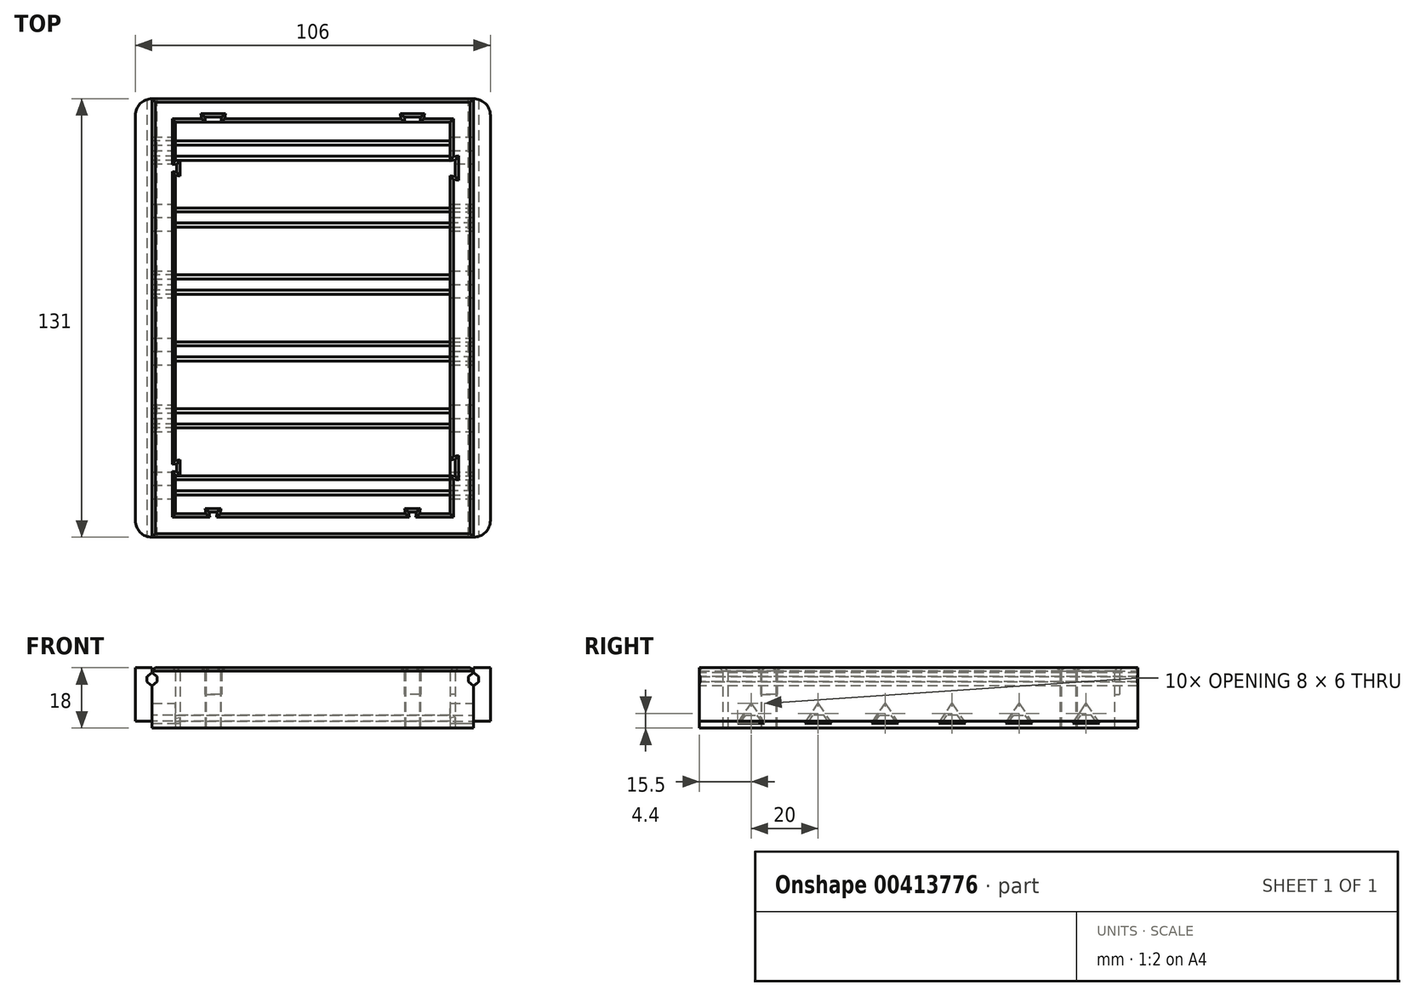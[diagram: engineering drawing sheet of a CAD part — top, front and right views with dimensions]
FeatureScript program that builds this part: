
annotation { "Feature Type Name" : "Feature", "Feature Type Description" : "" }
export const myFeature = defineFeature(function(context is Context, id is Id, definition is map)
    precondition{}
    {
        {
            var Q0;
            Q0=qCreatedBy(makeId("Top.planeOp"),FACE);
            var sketch = newSketch(context, id + "F0", { "sketchPlane" : qUnion([Q0])});
            skLineSegment(sketch, "E0.bottom", {"start": v(41, 58.5) * mm, "end": v(-41, 58.5) * mm});
            skLineSegment(sketch, "E0.top", {"start": v(41, -58.5) * mm, "end": v(-41, -58.5) * mm});
            skLineSegment(sketch, "E0.left", {"start": v(41, 58.5) * mm, "end": v(41, -58.5) * mm});
            skLineSegment(sketch, "E0.right", {"start": v(-41, 58.5) * mm, "end": v(-41, -58.5) * mm});
            skPoint(sketch, "E0.middle", {"position": v(0, 0) * mm});
            skPoint(sketch, "E1", {"position": v(41, 47) * mm});
            skPoint(sketch, "E2", {"position": v(41, 42.5) * mm});
            skLineSegment(sketch, "E3", {"start": v(41, 47) * mm, "end": v(41, 42.5) * mm});
            skLineSegment(sketch, "E4", {"start": v(42.5, 47.25) * mm, "end": v(42.5, 42.25) * mm});
            skPoint(sketch, "E5", {"position": v(41, 44.75) * mm});
            skPoint(sketch, "E6", {"position": v(42.5, 44.75) * mm});
            skLineSegment(sketch, "E7", {"start": v(42.5, 42.25) * mm, "end": v(41, 42.5) * mm});
            skLineSegment(sketch, "E8", {"start": v(41, 47) * mm, "end": v(42.5, 47.25) * mm});
            skLineSegment(sketch, "E9.MirrorCS", {"start": v(42.5, -42.25) * mm, "end": v(41, -42.5) * mm});
            skLineSegment(sketch, "E10.MirrorCS", {"start": v(42.5, -47.25) * mm, "end": v(42.5, -42.25) * mm});
            skLineSegment(sketch, "E11.MirrorCS", {"start": v(41, -47) * mm, "end": v(42.5, -47.25) * mm});
            skLineSegment(sketch, "E12.MirrorCS", {"start": v(41, -47) * mm, "end": v(41, -42.5) * mm});
            skLineSegment(sketch, "E13", {"start": v(-32, 58.5) * mm, "end": v(-32.25, 60) * mm});
            skLineSegment(sketch, "E14", {"start": v(-32.25, 60) * mm, "end": v(-27.25, 60) * mm});
            skLineSegment(sketch, "E15", {"start": v(-27.25, 60) * mm, "end": v(-27.5, 58.5) * mm});
            skPoint(sketch, "E16", {"position": v(-29.75, 60) * mm});
            skLineSegment(sketch, "E17", {"start": v(-32, 58.5) * mm, "end": v(-27.5, 58.5) * mm, "construction": true});
            skPoint(sketch, "E18", {"position": v(-29.75, 58.5) * mm});
            skLineSegment(sketch, "E19.MirrorCS", {"start": v(27.25, 60) * mm, "end": v(27.5, 58.5) * mm});
            skLineSegment(sketch, "E20.MirrorCS", {"start": v(32.25, 60) * mm, "end": v(27.25, 60) * mm});
            skLineSegment(sketch, "E21.MirrorCS", {"start": v(32, 58.5) * mm, "end": v(32.25, 60) * mm});
            skLineSegment(sketch, "E22.MirrorCS", {"start": v(32, 58.5) * mm, "end": v(27.5, 58.5) * mm, "construction": true});
            skLineSegment(sketch, "E23", {"start": v(-41, 46.9) * mm, "end": v(-39.7, 47.1) * mm});
            skLineSegment(sketch, "E24", {"start": v(-39.7, 47.1) * mm, "end": v(-39.7, 42.4) * mm});
            skLineSegment(sketch, "E25", {"start": v(-39.7, 42.4) * mm, "end": v(-41, 42.6) * mm});
            skPoint(sketch, "E26", {"position": v(-39.7, 44.75) * mm});
            skLineSegment(sketch, "E27", {"start": v(-41, 42.6) * mm, "end": v(-41, 46.9) * mm, "construction": true});
            skPoint(sketch, "E28", {"position": v(-41, 44.75) * mm});
            skLineSegment(sketch, "E29.MirrorCS", {"start": v(-39.7, -42.4) * mm, "end": v(-41, -42.6) * mm});
            skLineSegment(sketch, "E30.MirrorCS", {"start": v(-39.7, -47.1) * mm, "end": v(-39.7, -42.4) * mm});
            skLineSegment(sketch, "E31.MirrorCS", {"start": v(-41, -46.9) * mm, "end": v(-39.7, -47.1) * mm});
            skPoint(sketch, "E32", {"position": v(-29.75, -58.5) * mm});
            skLineSegment(sketch, "E33", {"start": v(-31.9, -58.5) * mm, "end": v(-27.6, -58.5) * mm, "construction": true});
            skLineSegment(sketch, "E34", {"start": v(-32.1, -57) * mm, "end": v(-27.4, -57) * mm});
            skPoint(sketch, "E35", {"position": v(-29.75, -57) * mm});
            skLineSegment(sketch, "E36", {"start": v(-32.1, -57) * mm, "end": v(-31.9, -58.5) * mm});
            skLineSegment(sketch, "E37", {"start": v(-27.6, -58.5) * mm, "end": v(-27.4, -57) * mm});
            skLineSegment(sketch, "E38.MirrorCS", {"start": v(27.6, -58.5) * mm, "end": v(27.4, -57) * mm});
            skLineSegment(sketch, "E39.MirrorCS", {"start": v(32.1, -57) * mm, "end": v(27.4, -57) * mm});
            skLineSegment(sketch, "E40.0", {"start": v(-48, 65.5) * mm, "end": v(-48, -65.5) * mm});
            skLineSegment(sketch, "E40.1", {"start": v(48, 65.5) * mm, "end": v(-48, 65.5) * mm});
            skLineSegment(sketch, "E40.2", {"start": v(48, 65.5) * mm, "end": v(48, -65.5) * mm});
            skLineSegment(sketch, "E40.3", {"start": v(48, -65.5) * mm, "end": v(-48, -65.5) * mm});
            skLineSegment(sketch, "E41.MirrorCS", {"start": v(31.9, -58.5) * mm, "end": v(27.6, -58.5) * mm, "construction": true});
            skLineSegment(sketch, "E42", {"start": v(32.1, -57) * mm, "end": v(31.9, -58.5) * mm});
            skSolve(sketch);
        }
        {
            var Q0;
            Q0 = qSketchRegion(id + "F0", true);
            var Q1;
            {var subQ0=sQuery(id+"F0.wireOp",EDGE,"E29.MirrorCS");Q1=makeQuery(id+"F0.imprint","IMPRINT",FACE,{"disambiguationData":[TD([[makeQuery(id+"F0.imprint","IMPRINT",EDGE,{"derivedFrom":subQ0}),1.0]])]});}
            var Q2;
            Q2=makeQuery(id+"F0.imprint","IMPRINT",FACE,{"disambiguationData":[TD([[makeQuery(id+"F0.imprint","IMPRINT",EDGE,{"derivedFrom":sQuery(id+"F0.wireOp",EDGE,"E34")}),-1.0]])]});
            var Q3;
            Q3=makeQuery(id+"F0.imprint","IMPRINT",FACE,{"disambiguationData":[TD([[makeQuery(id+"F0.imprint","IMPRINT",EDGE,{"derivedFrom":sQuery(id+"F0.wireOp",EDGE,"E39.MirrorCS")}),1.0]])]});
            var Q4;
            {var subQ0=sQuery(id+"F0.wireOp",EDGE,"E23");Q4=makeQuery(id+"F0.imprint","IMPRINT",FACE,{"disambiguationData":[TD([[makeQuery(id+"F0.imprint","IMPRINT",EDGE,{"derivedFrom":subQ0}),-1.0]])]});}
            extrude(context, id + "F1", {"entities" : qUnion([Q0, Q1, Q2, Q3, Q4]), "depth" : 8 * mm});
        }
        {
            var Q0;
            Q0=makeQuery(id+"F0.imprint","IMPRINT",FACE,{"disambiguationData":[TD([[makeQuery(id+"F0.imprint","IMPRINT",EDGE,{"derivedFrom":sQuery(id+"F0.wireOp",EDGE,"E4")}),1.0]])]});
            var Q1;
            Q1=makeQuery(id+"F0.imprint","IMPRINT",FACE,{"disambiguationData":[TD([[makeQuery(id+"F0.imprint","IMPRINT",EDGE,{"derivedFrom":sQuery(id+"F0.wireOp",EDGE,"E9.MirrorCS")}),1.0]])]});
            var Q2;
            {var subQ0=sQuery(id+"F0.wireOp",EDGE,"E19.MirrorCS");Q2=makeQuery(id+"F0.imprint","IMPRINT",FACE,{"disambiguationData":[TD([[makeQuery(id+"F0.imprint","IMPRINT",EDGE,{"derivedFrom":subQ0}),1.0]])]});}
            var Q3;
            {var subQ0=sQuery(id+"F0.wireOp",EDGE,"E13");Q3=makeQuery(id+"F0.imprint","IMPRINT",FACE,{"disambiguationData":[TD([[makeQuery(id+"F0.imprint","IMPRINT",EDGE,{"derivedFrom":subQ0}),-1.0]])]});}
            var Q4;
            Q4=makeQuery(id+"F0.imprint","IMPRINT",FACE,{"disambiguationData":[TD([[makeQuery(id+"F0.imprint","IMPRINT",EDGE,{"derivedFrom":sQuery(id+"F0.wireOp",EDGE,"E34")}),-1.0]])]});
            var Q5;
            {var subQ0=sQuery(id+"F0.wireOp",EDGE,"E29.MirrorCS");Q5=makeQuery(id+"F0.imprint","IMPRINT",FACE,{"disambiguationData":[TD([[makeQuery(id+"F0.imprint","IMPRINT",EDGE,{"derivedFrom":subQ0}),1.0]])]});}
            var Q6;
            Q6=makeQuery(id+"F0.imprint","IMPRINT",FACE,{"disambiguationData":[TD([[makeQuery(id+"F0.imprint","IMPRINT",EDGE,{"derivedFrom":sQuery(id+"F0.wireOp",EDGE,"E39.MirrorCS")}),1.0]])]});
            var Q7;
            Q7=makeQuery(id+"F0.imprint","IMPRINT",FACE,{"disambiguationData":[TD([[makeQuery(id+"F0.imprint","IMPRINT",EDGE,{"derivedFrom":sQuery(id+"F0.wireOp",EDGE,"E3")}),1.0]])]});
            var Q8;
            {var subQ1=sQuery(id+"F0.wireOp",EDGE,"E3");Q8=makeQuery(id+"F0.imprint","IMPRINT",FACE,{"disambiguationData":[TD([[makeQuery(id+"F0.imprint","IMPRINT",EDGE,{"derivedFrom":subQ1}),-1.0]])]});}
            var Q9;
            {var subQ0=sQuery(id+"F0.wireOp",EDGE,"E23");Q9=makeQuery(id+"F0.imprint","IMPRINT",FACE,{"disambiguationData":[TD([[makeQuery(id+"F0.imprint","IMPRINT",EDGE,{"derivedFrom":subQ0}),-1.0]])]});}
            extrude(context, id + "F2", {"entities" : qUnion([Q0, Q1, Q2, Q3, Q4, Q5, Q6, Q7, Q8, Q9]), "operationType" : NewBodyOperationType.ADD, "oppositeDirection" : true, "depth" : 8 * mm});
        }
        {
            var Q0;
            Q0=makeQuery(id+"F2.opExtrude","CAP_FACE",FACE,{"disambiguationData":[OSD([sQuery(id+"F0.wireOp",EDGE,"E40.0"),sQuery(id+"F0.wireOp",EDGE,"E40.1"),sQuery(id+"F0.wireOp",EDGE,"E40.2"),sQuery(id+"F0.wireOp",EDGE,"E40.3")])],"isStart":false});
            extrude(context, id + "F3", {"entities" : qUnion([Q0]), "operationType" : NewBodyOperationType.ADD, "depth" : 2 * mm});
        }
        {
            var Q0;
            {var subQ0=sQuery(id+"F0.wireOp",EDGE,"E40.2");Q0=makeQuery(id+"F2.boolean.opBoolean","MERGE",FACE,{"derivedFrom":[makeQuery(id+"F1.opExtrude","SWEPT_FACE",FACE,{"disambiguationData":[OSD([subQ0])]}),makeQuery(id+"F2.opExtrude","SWEPT_FACE",FACE,{"disambiguationData":[OSD([subQ0])]})]});}
            var sketch = newSketch(context, id + "F4", { "sketchPlane" : qUnion([Q0])});
            skLineSegment(sketch, "E43", {"start": v(-54, -8.6) * mm, "end": v(-50, -2.6) * mm});
            skLineSegment(sketch, "E44", {"start": v(-50, -2.6) * mm, "end": v(-46, -8.6) * mm});
            skLineSegment(sketch, "E45", {"start": v(-46, -8.6) * mm, "end": v(-54, -8.6) * mm});
            skPoint(sketch, "E46", {"position": v(-50, -8.6) * mm});
            skLineSegment(sketch, "E47.0", {"start": v(-52.88, -8) * mm, "end": v(-50, -3.68) * mm});
            skLineSegment(sketch, "E47.1", {"start": v(-47.12, -8) * mm, "end": v(-52.88, -8) * mm});
            skLineSegment(sketch, "E47.2", {"start": v(-50, -3.68) * mm, "end": v(-47.12, -8) * mm});
            skLineSegment(sketch, "E48.1.0.0", {"start": v(-30, -2.6) * mm, "end": v(-26, -8.6) * mm});
            skLineSegment(sketch, "E48.1.0.1", {"start": v(-30, -3.68) * mm, "end": v(-27.12, -8) * mm});
            skLineSegment(sketch, "E48.1.0.2", {"start": v(-34, -8.6) * mm, "end": v(-30, -2.6) * mm});
            skLineSegment(sketch, "E48.1.0.3", {"start": v(-32.88, -8) * mm, "end": v(-30, -3.68) * mm});
            skLineSegment(sketch, "E48.1.0.4", {"start": v(-27.12, -8) * mm, "end": v(-32.88, -8) * mm});
            skLineSegment(sketch, "E48.1.0.5", {"start": v(-26, -8.6) * mm, "end": v(-34, -8.6) * mm});
            skLineSegment(sketch, "E48.2.0.0", {"start": v(-10, -2.6) * mm, "end": v(-6, -8.6) * mm});
            skLineSegment(sketch, "E48.2.0.1", {"start": v(-10, -3.68) * mm, "end": v(-7.12, -8) * mm});
            skLineSegment(sketch, "E48.2.0.2", {"start": v(-14, -8.6) * mm, "end": v(-10, -2.6) * mm});
            skLineSegment(sketch, "E48.2.0.3", {"start": v(-12.88, -8) * mm, "end": v(-10, -3.68) * mm});
            skLineSegment(sketch, "E48.2.0.4", {"start": v(-7.12, -8) * mm, "end": v(-12.88, -8) * mm});
            skLineSegment(sketch, "E48.2.0.5", {"start": v(-6, -8.6) * mm, "end": v(-14, -8.6) * mm});
            skLineSegment(sketch, "E48.3.0.0", {"start": v(10, -2.6) * mm, "end": v(14, -8.6) * mm});
            skLineSegment(sketch, "E48.3.0.1", {"start": v(10, -3.68) * mm, "end": v(12.88, -8) * mm});
            skLineSegment(sketch, "E48.3.0.2", {"start": v(6, -8.6) * mm, "end": v(10, -2.6) * mm});
            skLineSegment(sketch, "E48.3.0.3", {"start": v(7.12, -8) * mm, "end": v(10, -3.68) * mm});
            skLineSegment(sketch, "E48.3.0.4", {"start": v(12.88, -8) * mm, "end": v(7.12, -8) * mm});
            skLineSegment(sketch, "E48.3.0.5", {"start": v(14, -8.6) * mm, "end": v(6, -8.6) * mm});
            skLineSegment(sketch, "E48.4.0.0", {"start": v(30, -2.6) * mm, "end": v(34, -8.6) * mm});
            skLineSegment(sketch, "E48.4.0.1", {"start": v(30, -3.68) * mm, "end": v(32.88, -8) * mm});
            skLineSegment(sketch, "E48.4.0.2", {"start": v(26, -8.6) * mm, "end": v(30, -2.6) * mm});
            skLineSegment(sketch, "E48.4.0.3", {"start": v(27.12, -8) * mm, "end": v(30, -3.68) * mm});
            skLineSegment(sketch, "E48.4.0.4", {"start": v(32.88, -8) * mm, "end": v(27.12, -8) * mm});
            skLineSegment(sketch, "E48.4.0.5", {"start": v(34, -8.6) * mm, "end": v(26, -8.6) * mm});
            skLineSegment(sketch, "E48.5.0.0", {"start": v(50, -2.6) * mm, "end": v(54, -8.6) * mm});
            skLineSegment(sketch, "E48.5.0.1", {"start": v(50, -3.68) * mm, "end": v(52.88, -8) * mm});
            skLineSegment(sketch, "E48.5.0.2", {"start": v(46, -8.6) * mm, "end": v(50, -2.6) * mm});
            skLineSegment(sketch, "E48.5.0.3", {"start": v(47.12, -8) * mm, "end": v(50, -3.68) * mm});
            skLineSegment(sketch, "E48.5.0.4", {"start": v(52.88, -8) * mm, "end": v(47.12, -8) * mm});
            skLineSegment(sketch, "E48.5.0.5", {"start": v(54, -8.6) * mm, "end": v(46, -8.6) * mm});
            skLineSegment(sketch, "E48.direction1", {"start": v(-46, -8.6) * mm, "end": v(-26, -8.6) * mm, "construction": true});
            skCircle(sketch, "E49", {"center": v(0, -4) * mm, "radius": 2.5 * mm});
            skPoint(sketch, "E49.centerSnap0", {"position": v(0, -10) * mm});
            skLineSegment(sketch, "E50", {"start": v(0.75, -1.62) * mm, "end": v(0.75, -6.38) * mm});
            skLineSegment(sketch, "E51", {"start": v(-0.75, -1.62) * mm, "end": v(-0.75, -6.38) * mm});
            skLineSegment(sketch, "E52", {"start": v(-65.5, -8) * mm, "end": v(65.5, -8) * mm});
            skLineSegment(sketch, "E53", {"start": v(-54, -8.6) * mm, "end": v(-65.5, -8.6) * mm, "construction": true});
            skLineSegment(sketch, "E54", {"start": v(54, -8.6) * mm, "end": v(65.5, -8.6) * mm, "construction": true});
            skSolve(sketch);
        }
        {
            var Q0;
            Q0=makeQuery(id+"F4.imprint","IMPRINT",FACE,{"disambiguationData":[TD([[makeQuery(id+"F4.imprint","IMPRINT",EDGE,{"derivedFrom":sQuery(id+"F4.wireOp",EDGE,"E43")}),-1.0]])]});
            var Q1;
            Q1=makeQuery(id+"F4.imprint","IMPRINT",FACE,{"disambiguationData":[TD([[makeQuery(id+"F4.imprint","IMPRINT",EDGE,{"derivedFrom":sQuery(id+"F4.wireOp",EDGE,"E47.0")}),-1.0]])]});
            var Q2;
            Q2=makeQuery(id+"F4.imprint","IMPRINT",FACE,{"disambiguationData":[TD([[makeQuery(id+"F4.imprint","IMPRINT",EDGE,{"derivedFrom":sQuery(id+"F4.wireOp",EDGE,"E48.1.0.0")}),-1.0]])]});
            var Q3;
            Q3=makeQuery(id+"F4.imprint","IMPRINT",FACE,{"disambiguationData":[TD([[makeQuery(id+"F4.imprint","IMPRINT",EDGE,{"derivedFrom":sQuery(id+"F4.wireOp",EDGE,"E48.1.0.1")}),-1.0]])]});
            var Q4;
            Q4=makeQuery(id+"F4.imprint","IMPRINT",FACE,{"disambiguationData":[TD([[makeQuery(id+"F4.imprint","IMPRINT",EDGE,{"derivedFrom":sQuery(id+"F4.wireOp",EDGE,"E48.2.0.0")}),-1.0]])]});
            var Q5;
            Q5=makeQuery(id+"F4.imprint","IMPRINT",FACE,{"disambiguationData":[TD([[makeQuery(id+"F4.imprint","IMPRINT",EDGE,{"derivedFrom":sQuery(id+"F4.wireOp",EDGE,"E48.2.0.1")}),-1.0]])]});
            var Q6;
            Q6=makeQuery(id+"F4.imprint","IMPRINT",FACE,{"disambiguationData":[TD([[makeQuery(id+"F4.imprint","IMPRINT",EDGE,{"derivedFrom":sQuery(id+"F4.wireOp",EDGE,"E48.3.0.1")}),-1.0]])]});
            var Q7;
            Q7=makeQuery(id+"F4.imprint","IMPRINT",FACE,{"disambiguationData":[TD([[makeQuery(id+"F4.imprint","IMPRINT",EDGE,{"derivedFrom":sQuery(id+"F4.wireOp",EDGE,"E48.3.0.0")}),-1.0]])]});
            var Q8;
            Q8=makeQuery(id+"F4.imprint","IMPRINT",FACE,{"disambiguationData":[TD([[makeQuery(id+"F4.imprint","IMPRINT",EDGE,{"derivedFrom":sQuery(id+"F4.wireOp",EDGE,"E48.5.0.1")}),-1.0]])]});
            var Q9;
            Q9=makeQuery(id+"F4.imprint","IMPRINT",FACE,{"disambiguationData":[TD([[makeQuery(id+"F4.imprint","IMPRINT",EDGE,{"derivedFrom":sQuery(id+"F4.wireOp",EDGE,"E48.5.0.0")}),-1.0]])]});
            var Q10;
            Q10=makeQuery(id+"F4.imprint","IMPRINT",FACE,{"disambiguationData":[TD([[makeQuery(id+"F4.imprint","IMPRINT",EDGE,{"derivedFrom":sQuery(id+"F4.wireOp",EDGE,"E48.4.0.1")}),-1.0]])]});
            var Q11;
            Q11=makeQuery(id+"F4.imprint","IMPRINT",FACE,{"disambiguationData":[TD([[makeQuery(id+"F4.imprint","IMPRINT",EDGE,{"derivedFrom":sQuery(id+"F4.wireOp",EDGE,"E48.4.0.0")}),-1.0]])]});
            var Q12;
            {var subQ0=sQuery(id+"F4.wireOp",EDGE,"E51");Q12=makeQuery(id+"F4.imprint","IMPRINT",FACE,{"disambiguationData":[TD([[makeQuery(id+"F4.imprint","IMPRINT",EDGE,{"derivedFrom":subQ0}),-1.0]])]});}
            var Q13;
            {var subQ0=sQuery(id+"F4.wireOp",EDGE,"E50");Q13=makeQuery(id+"F4.imprint","IMPRINT",FACE,{"disambiguationData":[TD([[makeQuery(id+"F4.imprint","IMPRINT",EDGE,{"derivedFrom":subQ0}),1.0]])]});}
            var Q14;
            {var subQ0=sQuery(id+"F4.wireOp",EDGE,"E50");Q14=makeQuery(id+"F4.imprint","IMPRINT",FACE,{"disambiguationData":[TD([[makeQuery(id+"F4.imprint","IMPRINT",EDGE,{"derivedFrom":subQ0}),-1.0]])]});}
            extrude(context, id + "F5", {"entities" : qUnion([Q0, Q1, Q2, Q3, Q4, Q5, Q6, Q7, Q8, Q9, Q10, Q11, Q12, Q13, Q14]), "operationType" : NewBodyOperationType.REMOVE, "endBound" : BoundingType.THROUGH_ALL, "oppositeDirection" : true, "depth" : 104.4 * mm});
        }
        {
            var Q0;
            {var subQ0=sQuery(id+"F4.wireOp",EDGE,"E47.0");Q0=makeQuery(id+"F4.imprint","IMPRINT",FACE,{"disambiguationData":[TD([[makeQuery(id+"F4.imprint","IMPRINT",EDGE,{"derivedFrom":subQ0}),1.0]])]});}
            var Q1;
            {var subQ5=sQuery(id+"F4.wireOp",EDGE,"E48.5.0.1");Q1=makeQuery(id+"F4.imprint","IMPRINT",FACE,{"disambiguationData":[TD([[makeQuery(id+"F4.imprint","IMPRINT",EDGE,{"derivedFrom":subQ5}),1.0]])]});}
            var Q2;
            {var subQ0=sQuery(id+"F4.wireOp",EDGE,"E48.5.0.1");Q2=makeQuery(id+"F4.imprint","IMPRINT",FACE,{"disambiguationData":[TD([[makeQuery(id+"F4.imprint","IMPRINT",EDGE,{"derivedFrom":subQ0}),-1.0]])]});}
            var Q3;
            {var subQ0=sQuery(id+"F4.wireOp",EDGE,"E48.4.0.1");Q3=makeQuery(id+"F4.imprint","IMPRINT",FACE,{"disambiguationData":[TD([[makeQuery(id+"F4.imprint","IMPRINT",EDGE,{"derivedFrom":subQ0}),-1.0]])]});}
            var Q4;
            {var subQ5=sQuery(id+"F4.wireOp",EDGE,"E48.4.0.1");Q4=makeQuery(id+"F4.imprint","IMPRINT",FACE,{"disambiguationData":[TD([[makeQuery(id+"F4.imprint","IMPRINT",EDGE,{"derivedFrom":subQ5}),1.0]])]});}
            var Q5;
            {var subQ0=sQuery(id+"F4.wireOp",EDGE,"E48.3.0.1");Q5=makeQuery(id+"F4.imprint","IMPRINT",FACE,{"disambiguationData":[TD([[makeQuery(id+"F4.imprint","IMPRINT",EDGE,{"derivedFrom":subQ0}),-1.0]])]});}
            var Q6;
            {var subQ6=sQuery(id+"F4.wireOp",EDGE,"E48.3.0.1");Q6=makeQuery(id+"F4.imprint","IMPRINT",FACE,{"disambiguationData":[TD([[makeQuery(id+"F4.imprint","IMPRINT",EDGE,{"derivedFrom":subQ6}),1.0]])]});}
            var Q7;
            {var subQ0=sQuery(id+"F4.wireOp",EDGE,"E48.2.0.1");Q7=makeQuery(id+"F4.imprint","IMPRINT",FACE,{"disambiguationData":[TD([[makeQuery(id+"F4.imprint","IMPRINT",EDGE,{"derivedFrom":subQ0}),-1.0]])]});}
            var Q8;
            {var subQ5=sQuery(id+"F4.wireOp",EDGE,"E48.2.0.1");Q8=makeQuery(id+"F4.imprint","IMPRINT",FACE,{"disambiguationData":[TD([[makeQuery(id+"F4.imprint","IMPRINT",EDGE,{"derivedFrom":subQ5}),1.0]])]});}
            var Q9;
            {var subQ0=sQuery(id+"F4.wireOp",EDGE,"E48.1.0.1");Q9=makeQuery(id+"F4.imprint","IMPRINT",FACE,{"disambiguationData":[TD([[makeQuery(id+"F4.imprint","IMPRINT",EDGE,{"derivedFrom":subQ0}),-1.0]])]});}
            var Q10;
            {var subQ5=sQuery(id+"F4.wireOp",EDGE,"E48.1.0.1");Q10=makeQuery(id+"F4.imprint","IMPRINT",FACE,{"disambiguationData":[TD([[makeQuery(id+"F4.imprint","IMPRINT",EDGE,{"derivedFrom":subQ5}),1.0]])]});}
            var Q11;
            {var subQ0=sQuery(id+"F4.wireOp",EDGE,"E47.0");Q11=makeQuery(id+"F4.imprint","IMPRINT",FACE,{"disambiguationData":[TD([[makeQuery(id+"F4.imprint","IMPRINT",EDGE,{"derivedFrom":subQ0}),-1.0]])]});}
            var Q12;
            {var subQ15=sQuery(id+"F0.wireOp",EDGE,"E40.2");var subQ43=makeQuery(id+"F1.opExtrude","CAP_EDGE",EDGE,{"disambiguationData":[OSD([subQ15])],"isStart":false});Q12=makeQuery(id+"F4.imprint","IMPRINT",FACE,{"disambiguationData":[TD([[makeQuery(id+"F4.imprint","IMPRINT",EDGE,{"derivedFrom":subQ43}),1.0]])]});}
            var Q13;
            {var subQ0=sQuery(id+"F4.wireOp",EDGE,"E50");var subQ1=sQuery(id+"F4.wireOp",EDGE,"E49");var subQ2=makeQuery(id+"F4.imprint","INTERSECT",VERTEX,{"disambiguationData":[OD(0.0)],"derivedFrom":[subQ1,subQ0]});Q13=makeQuery(id+"F4.imprint","IMPRINT",FACE,{"disambiguationData":[TD([[makeQuery(id+"F4.imprint","IMPRINT",EDGE,{"disambiguationData":[TD([[subQ2,-1.0]])],"derivedFrom":subQ1}),1.0]])]});}
            var Q14;
            {var subQ0=sQuery(id+"F4.wireOp",EDGE,"E50");var subQ1=sQuery(id+"F4.wireOp",EDGE,"E49");var subQ2=makeQuery(id+"F4.imprint","INTERSECT",VERTEX,{"disambiguationData":[OD(1.0)],"derivedFrom":[subQ1,subQ0]});Q14=makeQuery(id+"F4.imprint","IMPRINT",FACE,{"disambiguationData":[TD([[makeQuery(id+"F4.imprint","IMPRINT",EDGE,{"disambiguationData":[TD([[subQ2,1.0]])],"derivedFrom":subQ1}),1.0]])]});}
            extrude(context, id + "F6", {"entities" : qUnion([Q0, Q1, Q2, Q3, Q4, Q5, Q6, Q7, Q8, Q9, Q10, Q11, Q12, Q13, Q14]), "depth" : 5 * mm});
        }
        {
            var Q0;
            Q0=makeQuery(id+"F4.imprint","IMPRINT",FACE,{"disambiguationData":[TD([[makeQuery(id+"F4.imprint","IMPRINT",EDGE,{"derivedFrom":sQuery(id+"F4.wireOp",EDGE,"E48.2.0.1")}),-1.0]])]});
            var Q1;
            Q1=makeQuery(id+"F4.imprint","IMPRINT",FACE,{"disambiguationData":[TD([[makeQuery(id+"F4.imprint","IMPRINT",EDGE,{"derivedFrom":sQuery(id+"F4.wireOp",EDGE,"E48.4.0.1")}),-1.0]])]});
            var Q2;
            Q2=makeQuery(id+"F4.imprint","IMPRINT",FACE,{"disambiguationData":[TD([[makeQuery(id+"F4.imprint","IMPRINT",EDGE,{"derivedFrom":sQuery(id+"F4.wireOp",EDGE,"E47.0")}),-1.0]])]});
            var Q3;
            {var subQ0=sQuery(id+"F0.wireOp",EDGE,"E0.right");Q3=makeQuery(id+"F1.opExtrude","SWEPT_FACE",FACE,{"disambiguationData":[OSD([subQ0]),TDD([makeQuery(id+"F0.imprint","IMPRINT",EDGE,{"disambiguationData":[TD([[makeQuery(id+"F0.imprint","INTERSECT",VERTEX,{"derivedFrom":[subQ0,sQuery(id+"F0.wireOp",EDGE,"E25")]}),-1.0]])],"derivedFrom":subQ0})])]});}
            extrude(context, id + "F7", {"entities" : qUnion([Q0, Q1, Q2]), "operationType" : NewBodyOperationType.ADD, "endBound" : BoundingType.UP_TO_SURFACE, "oppositeDirection" : true, "endBoundEntityFace" : qUnion([Q3]), "depth" : 25 * mm});
        }
        {
            var Q0;
            Q0=makeQuery(id+"F6.opExtrude","SWEPT_FACE",FACE,{"disambiguationData":[OSD([sQuery(id+"F0.wireOp",EDGE,"E40.2"),sQuery(id+"F0.wireOp",EDGE,"E40.3")])]});
            var sketch = newSketch(context, id + "F8", { "sketchPlane" : qUnion([Q0])});
            skLineSegment(sketch, "E55", {"start": v(48, 6.58) * mm, "end": v(50.5, 4.58) * mm});
            skLineSegment(sketch, "E56", {"start": v(50.5, 4.58) * mm, "end": v(48, 2.58) * mm});
            skLineSegment(sketch, "E57", {"start": v(48, 2.58) * mm, "end": v(45.5, 4.58) * mm});
            skLineSegment(sketch, "E58", {"start": v(45.5, 4.58) * mm, "end": v(48, 6.58) * mm});
            skLineSegment(sketch, "E59", {"start": v(50.5, 4.58) * mm, "end": v(48, 4.58) * mm, "construction": true});
            skLineSegment(sketch, "E60", {"start": v(48, 4.58) * mm, "end": v(45.5, 4.58) * mm, "construction": true});
            skSolve(sketch);
        }
        {
            var Q0;
            Q0 = qSketchRegion(id + "F8", true);
            extrude(context, id + "F9", {"entities" : qUnion([Q0]), "endBound" : BoundingType.THROUGH_ALL, "oppositeDirection" : true, "depth" : 25 * mm});
        }
        {
            var Q0;
            Q0=makeQuery(id+"F9.opExtrude","SWEPT_EDGE",EDGE,{"disambiguationData":[OSD([sQuery(id+"F8.wireOp",EDGE,"E55"),sQuery(id+"F8.wireOp",EDGE,"E56")])]});
            var Q1;
            Q1=makeQuery(id+"F9.opExtrude","SWEPT_EDGE",EDGE,{"disambiguationData":[OSD([sQuery(id+"F8.wireOp",EDGE,"E57"),sQuery(id+"F8.wireOp",EDGE,"E58")])]});
            chamfer(context, id + "F10", {"entities" : qUnion([Q0, Q1]), "width" : 1 * mm, "tangentPropagation" : true});
        }
        {
            var Q0;
            Q0=makeQuery(id+"F6.opExtrude","CAP_EDGE",EDGE,{"disambiguationData":[OSD([sQuery(id+"F0.wireOp",EDGE,"E40.2"),sQuery(id+"F0.wireOp",EDGE,"E40.3")])],"isStart":false});
            var Q1;
            Q1=makeQuery(id+"F6.opExtrude","CAP_EDGE",EDGE,{"disambiguationData":[OSD([sQuery(id+"F0.wireOp",EDGE,"E40.1"),sQuery(id+"F0.wireOp",EDGE,"E40.2")])],"isStart":false});
            fillet(context, id + "F11", {"entities" : qUnion([Q0, Q1]), "radius" : 5 * mm, "tangentPropagation" : true, "allowEdgeOverflow" : false});
        }
        {
            var Q0;
            Q0=makeQuery(id+"F7.opExtrude","SWEPT_EDGE",EDGE,{"disambiguationData":[OSD([sQuery(id+"F4.wireOp",EDGE,"E48.2.0.1"),sQuery(id+"F4.wireOp",EDGE,"E48.2.0.3")])]});
            var Q1;
            Q1=makeQuery(id+"F7.opExtrude","SWEPT_EDGE",EDGE,{"disambiguationData":[OSD([sQuery(id+"F4.wireOp",EDGE,"E48.4.0.1"),sQuery(id+"F4.wireOp",EDGE,"E48.4.0.3")])]});
            var Q2;
            Q2=makeQuery(id+"F7.opExtrude","SWEPT_EDGE",EDGE,{"disambiguationData":[OSD([sQuery(id+"F4.wireOp",EDGE,"E47.0"),sQuery(id+"F4.wireOp",EDGE,"E47.2")])]});
            chamfer(context, id + "F12", {"entities" : qUnion([Q0, Q1, Q2]), "width" : 2 * mm, "tangentPropagation" : true});
        }
        {
            var Q0;
            Q0=qCreatedBy(makeId("Right.planeOp"),FACE);
            var sketch = newSketch(context, id + "F13", { "sketchPlane" : qUnion([Q0])});
            skLineSegment(sketch, "E61", {"start": v(0, 0) * mm, "end": v(0, 59.99) * mm, "construction": true});
            skSolve(sketch);
        }
        {
            var Q0;
            Q0=makeQuery(id+"F6.opExtrude","SWEPT_BODY",BODY,{"disambiguationData":[OSD([sQuery(id+"F0.wireOp",EDGE,"E40.1"),sQuery(id+"F0.wireOp",EDGE,"E40.2"),sQuery(id+"F0.wireOp",EDGE,"E40.3")])]});
            var Q1;
            Q1=sQuery(id+"F13.wireOp",EDGE,"E61");
            transform(context, id + "F14", {"entities" : qUnion([Q0]), "transformType" : TransformType.ROTATION, "transformAxis" : qUnion([Q1]), "angle" : 180 * degree, "makeCopy" : true});
        }
        {
            var Q0;
            Q0=makeQuery(id+"F1.opExtrude","CAP_FACE",FACE,{"disambiguationData":[OSD([sQuery(id+"F0.wireOp",EDGE,"E0.bottom"),sQuery(id+"F0.wireOp",EDGE,"E0.top"),sQuery(id+"F0.wireOp",EDGE,"E0.left"),sQuery(id+"F0.wireOp",EDGE,"E0.right"),sQuery(id+"F0.wireOp",EDGE,"E4"),sQuery(id+"F0.wireOp",EDGE,"E7"),sQuery(id+"F0.wireOp",EDGE,"E8"),sQuery(id+"F0.wireOp",EDGE,"E9.MirrorCS"),sQuery(id+"F0.wireOp",EDGE,"E10.MirrorCS"),sQuery(id+"F0.wireOp",EDGE,"E11.MirrorCS"),sQuery(id+"F0.wireOp",EDGE,"E13"),sQuery(id+"F0.wireOp",EDGE,"E14"),sQuery(id+"F0.wireOp",EDGE,"E15"),sQuery(id+"F0.wireOp",EDGE,"E19.MirrorCS"),sQuery(id+"F0.wireOp",EDGE,"E20.MirrorCS"),sQuery(id+"F0.wireOp",EDGE,"E21.MirrorCS"),sQuery(id+"F0.wireOp",EDGE,"E23"),sQuery(id+"F0.wireOp",EDGE,"E24"),sQuery(id+"F0.wireOp",EDGE,"E25"),sQuery(id+"F0.wireOp",EDGE,"E29.MirrorCS"),sQuery(id+"F0.wireOp",EDGE,"E30.MirrorCS"),sQuery(id+"F0.wireOp",EDGE,"E31.MirrorCS"),sQuery(id+"F0.wireOp",EDGE,"E34"),sQuery(id+"F0.wireOp",EDGE,"E36"),sQuery(id+"F0.wireOp",EDGE,"E37"),sQuery(id+"F0.wireOp",EDGE,"E39.MirrorCS"),sQuery(id+"F0.wireOp",EDGE,"E40.0"),sQuery(id+"F0.wireOp",EDGE,"E40.1"),sQuery(id+"F0.wireOp",EDGE,"E40.2"),sQuery(id+"F0.wireOp",EDGE,"E40.3"),sQuery(id+"F0.wireOp",EDGE,"E38.MirrorCS"),sQuery(id+"F0.wireOp",EDGE,"E42")])],"isStart":false});
            chamfer(context, id + "F15", {"entities" : qUnion([Q0]), "width" : 1 * mm, "tangentPropagation" : true});
        }
        {
            var Q0;
            Q0=makeQuery(id+"F9.opExtrude","SWEPT_BODY",BODY,{"disambiguationData":[OSD([sQuery(id+"F8.wireOp",EDGE,"E55"),sQuery(id+"F8.wireOp",EDGE,"E56"),sQuery(id+"F8.wireOp",EDGE,"E57"),sQuery(id+"F8.wireOp",EDGE,"E58")])]});
            var Q1;
            Q1=qCreatedBy(makeId("Right.planeOp"),FACE);
            mirror(context, id + "F16", {"entities" : qUnion([Q0]), "mirrorPlane" : qUnion([Q1])});
        }
        {
            var Q0;
            Q0=makeQuery(id+"F9.opExtrude","SWEPT_BODY",BODY,{"disambiguationData":[OSD([sQuery(id+"F8.wireOp",EDGE,"E55"),sQuery(id+"F8.wireOp",EDGE,"E56"),sQuery(id+"F8.wireOp",EDGE,"E57"),sQuery(id+"F8.wireOp",EDGE,"E58")])]});
            var Q1;
            Q1=makeQuery(id+"F16.opPattern","COPY",BODY,{"derivedFrom":makeQuery(id+"F9.opExtrude","SWEPT_BODY",BODY,{"disambiguationData":[OSD([sQuery(id+"F8.wireOp",EDGE,"E55"),sQuery(id+"F8.wireOp",EDGE,"E56"),sQuery(id+"F8.wireOp",EDGE,"E57"),sQuery(id+"F8.wireOp",EDGE,"E58")])]}),"instanceName":"1"});
            var Q2;
            Q2=makeQuery(id+"F1.opExtrude","SWEPT_BODY",BODY,{"disambiguationData":[OSD([sQuery(id+"F0.wireOp",EDGE,"E0.bottom"),sQuery(id+"F0.wireOp",EDGE,"E0.top"),sQuery(id+"F0.wireOp",EDGE,"E0.left"),sQuery(id+"F0.wireOp",EDGE,"E0.right"),sQuery(id+"F0.wireOp",EDGE,"E4"),sQuery(id+"F0.wireOp",EDGE,"E7"),sQuery(id+"F0.wireOp",EDGE,"E8"),sQuery(id+"F0.wireOp",EDGE,"E9.MirrorCS"),sQuery(id+"F0.wireOp",EDGE,"E10.MirrorCS"),sQuery(id+"F0.wireOp",EDGE,"E11.MirrorCS"),sQuery(id+"F0.wireOp",EDGE,"E13"),sQuery(id+"F0.wireOp",EDGE,"E14"),sQuery(id+"F0.wireOp",EDGE,"E15"),sQuery(id+"F0.wireOp",EDGE,"E19.MirrorCS"),sQuery(id+"F0.wireOp",EDGE,"E20.MirrorCS"),sQuery(id+"F0.wireOp",EDGE,"E21.MirrorCS"),sQuery(id+"F0.wireOp",EDGE,"E23"),sQuery(id+"F0.wireOp",EDGE,"E24"),sQuery(id+"F0.wireOp",EDGE,"E25"),sQuery(id+"F0.wireOp",EDGE,"E29.MirrorCS"),sQuery(id+"F0.wireOp",EDGE,"E30.MirrorCS"),sQuery(id+"F0.wireOp",EDGE,"E31.MirrorCS"),sQuery(id+"F0.wireOp",EDGE,"E34"),sQuery(id+"F0.wireOp",EDGE,"E36"),sQuery(id+"F0.wireOp",EDGE,"E37"),sQuery(id+"F0.wireOp",EDGE,"E39.MirrorCS"),sQuery(id+"F0.wireOp",EDGE,"E40.0"),sQuery(id+"F0.wireOp",EDGE,"E40.1"),sQuery(id+"F0.wireOp",EDGE,"E40.2"),sQuery(id+"F0.wireOp",EDGE,"E40.3"),sQuery(id+"F0.wireOp",EDGE,"E38.MirrorCS"),sQuery(id+"F0.wireOp",EDGE,"E42")])]});
            var Q3;
            Q3=makeQuery(id+"F6.opExtrude","SWEPT_BODY",BODY,{"disambiguationData":[OSD([sQuery(id+"F0.wireOp",EDGE,"E40.1"),sQuery(id+"F0.wireOp",EDGE,"E40.2"),sQuery(id+"F0.wireOp",EDGE,"E40.3"),sQuery(id+"F4.wireOp",EDGE,"E49"),sQuery(id+"F4.wireOp",EDGE,"E50"),sQuery(id+"F4.wireOp",EDGE,"E51"),sQuery(id+"F4.wireOp",EDGE,"E52")])]});
            var Q4;
            Q4=makeQuery(id+"F14.opPattern","COPY",BODY,{"derivedFrom":makeQuery(id+"F6.opExtrude","SWEPT_BODY",BODY,{"disambiguationData":[OSD([sQuery(id+"F0.wireOp",EDGE,"E40.1"),sQuery(id+"F0.wireOp",EDGE,"E40.2"),sQuery(id+"F0.wireOp",EDGE,"E40.3"),sQuery(id+"F4.wireOp",EDGE,"E49"),sQuery(id+"F4.wireOp",EDGE,"E50"),sQuery(id+"F4.wireOp",EDGE,"E51"),sQuery(id+"F4.wireOp",EDGE,"E52")])]}),"instanceName":"1"});
            booleanBodies(context, id + "F17", {"operationType" : BooleanOperationType.SUBTRACTION, "tools" : qUnion([Q0, Q1]), "targets" : qUnion([Q2, Q3, Q4])});
        }
    });
